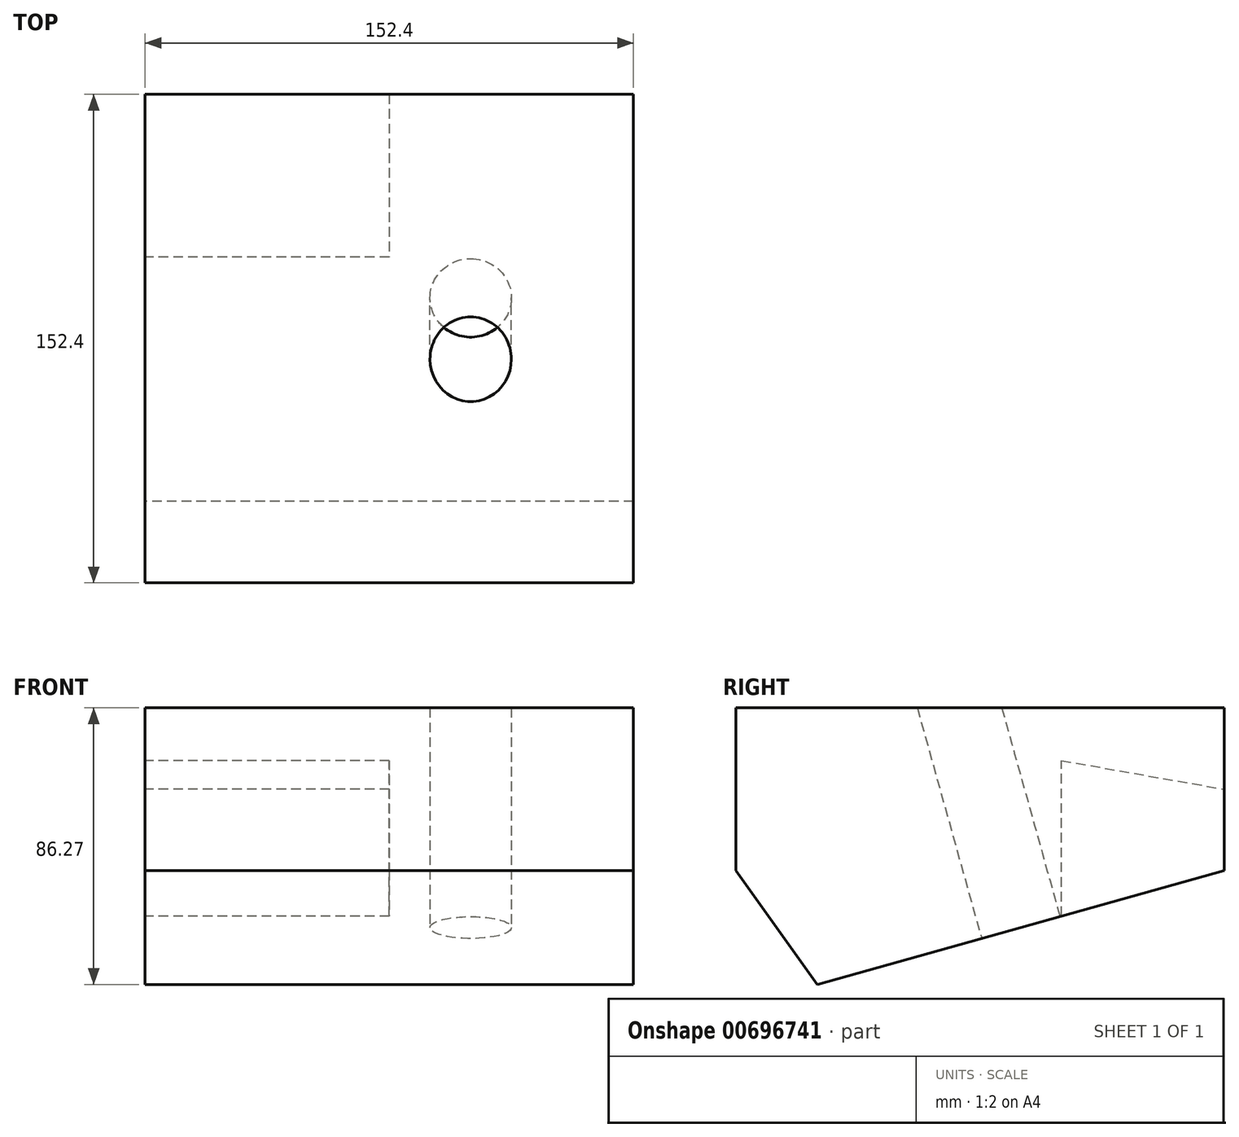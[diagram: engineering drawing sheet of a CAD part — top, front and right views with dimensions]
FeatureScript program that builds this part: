
annotation { "Feature Type Name" : "Feature", "Feature Type Description" : "" }
export const myFeature = defineFeature(function(context is Context, id is Id, definition is map)
    precondition{}
    {
        {
            var Q0;
            Q0=qCreatedBy(makeId("Right.planeOp"),FACE);
            var sketch = newSketch(context, id + "F0", { "sketchPlane" : qUnion([Q0])});
            skLineSegment(sketch, "E0", {"start": v(0, 50.8) * mm, "end": v(152.4, 50.8) * mm});
            skLineSegment(sketch, "E1", {"start": v(152.4, 50.8) * mm, "end": v(152.4, 0) * mm});
            skLineSegment(sketch, "E2", {"start": v(0, 50.8) * mm, "end": v(0, 0) * mm});
            skLineSegment(sketch, "E3", {"start": v(25.4, -35.47) * mm, "end": v(0, 0) * mm});
            skLineSegment(sketch, "E4", {"start": v(152.4, 0) * mm, "end": v(25.4, -35.47) * mm});
            skSolve(sketch);
        }
        {
            var Q0;
            Q0=makeQuery(id+"F0.imprint","IMPRINT",FACE,{"disambiguationData":[TD([[makeQuery(id+"F0.imprint","IMPRINT",EDGE,{"derivedFrom":sQuery(id+"F0.wireOp",EDGE,"E0")}),-1.0]])]});
            extrude(context, id + "F1", {"entities" : qUnion([Q0]), "depth" : 152.4 * mm, "offsetDistance" : 25.4 * mm});
        }
        {
            var Q0;
            Q0=makeQuery(id+"F1.opExtrude","SWEPT_FACE",FACE,{"disambiguationData":[OSD([sQuery(id+"F0.wireOp",EDGE,"E4")])]});
            var sketch = newSketch(context, id + "F2", { "sketchPlane" : qUnion([Q0])});
            skCircle(sketch, "E5", {"center": v(101.6, -80.85) * mm, "radius": 12.7 * mm});
            skPoint(sketch, "E6", {"position": v(152.4, -80.85) * mm});
            skSolve(sketch);
        }
        {
            var Q0;
            Q0=makeQuery(id+"F2.imprint","IMPRINT",FACE,{"disambiguationData":[TD([[makeQuery(id+"F2.imprint","IMPRINT",EDGE,{"derivedFrom":sQuery(id+"F2.wireOp",EDGE,"E5")}),1.0]])]});
            extrude(context, id + "F3", {"entities" : qUnion([Q0]), "operationType" : NewBodyOperationType.REMOVE, "endBound" : BoundingType.UP_TO_NEXT, "oppositeDirection" : true, "depth" : 25.4 * mm, "offsetDistance" : 25.4 * mm});
        }
        {
            var Q0;
            Q0=makeQuery(id+"F1.opExtrude","CAP_FACE",FACE,{"disambiguationData":[OSD([sQuery(id+"F0.wireOp",EDGE,"E0"),sQuery(id+"F0.wireOp",EDGE,"E1"),sQuery(id+"F0.wireOp",EDGE,"E2"),sQuery(id+"F0.wireOp",EDGE,"E3"),sQuery(id+"F0.wireOp",EDGE,"E4")])],"isStart":true});
            var sketch = newSketch(context, id + "F4", { "sketchPlane" : qUnion([Q0])});
            skLineSegment(sketch, "E7", {"start": v(-101.6, -14.19) * mm, "end": v(-101.6, 34.36) * mm});
            skLineSegment(sketch, "E8", {"start": v(-101.6, 34.36) * mm, "end": v(-152.4, 25.4) * mm});
            skSolve(sketch);
        }
        {
            var Q0;
            {var subQ0=sQuery(id+"F4.wireOp",EDGE,"E7");Q0=makeQuery(id+"F4.imprint","IMPRINT",FACE,{"disambiguationData":[TD([[makeQuery(id+"F4.imprint","IMPRINT",EDGE,{"derivedFrom":subQ0}),1.0]])]});}
            extrude(context, id + "F5", {"entities" : qUnion([Q0]), "operationType" : NewBodyOperationType.REMOVE, "oppositeDirection" : true, "depth" : 76.2 * mm, "offsetDistance" : 25.4 * mm});
        }
    });
